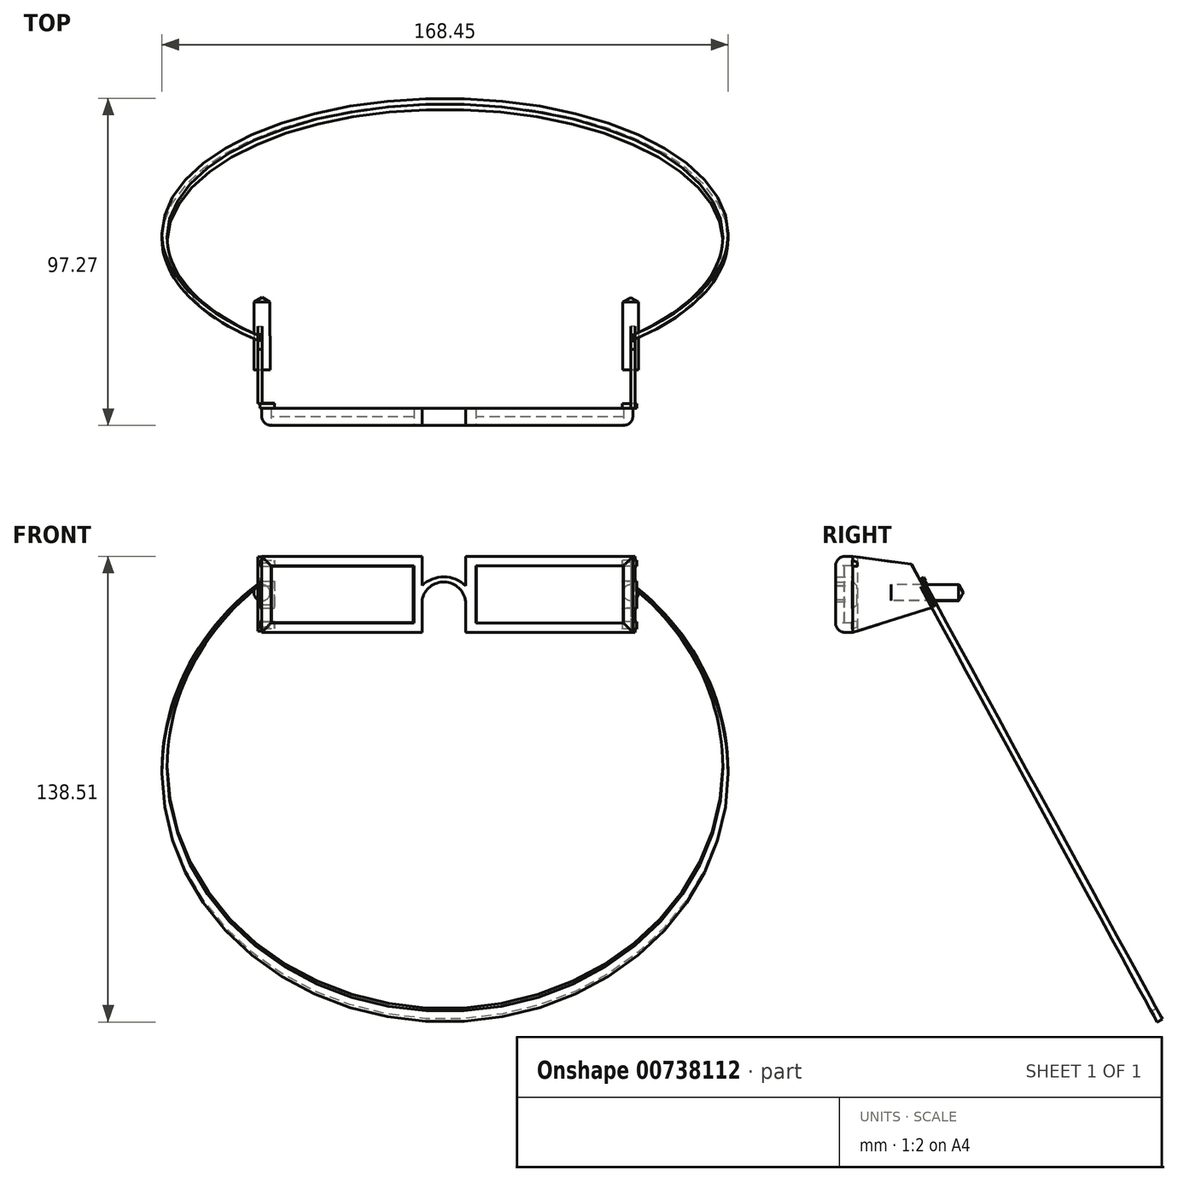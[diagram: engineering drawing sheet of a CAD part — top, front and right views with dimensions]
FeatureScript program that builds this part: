
annotation { "Feature Type Name" : "Feature", "Feature Type Description" : "" }
export const myFeature = defineFeature(function(context is Context, id is Id, definition is map)
    precondition{}
    {
        {
            var Q0;
            Q0=qCreatedBy(makeId("Front.planeOp"),FACE);
            var sketch = newSketch(context, id + "F0", { "sketchPlane" : qUnion([Q0])});
            skLineSegment(sketch, "E0.bottom", {"start": v(-53.68, 22.6) * mm, "end": v(-5.9, 22.6) * mm});
            skLineSegment(sketch, "E0.top", {"start": v(-53.68, 0) * mm, "end": v(-5.9, 0) * mm});
            skLineSegment(sketch, "E0.left", {"start": v(-53.68, 22.6) * mm, "end": v(-53.68, 0) * mm});
            skLineSegment(sketch, "E0.right", {"start": v(-5.9, 22.6) * mm, "end": v(-5.9, 0) * mm});
            skPoint(sketch, "E1.firstSnap0", {"position": v(-29.79, 22.6) * mm});
            skLineSegment(sketch, "E1.bottom", {"start": v(7.05, 22.6) * mm, "end": v(56.84, 22.6) * mm});
            skLineSegment(sketch, "E1.top", {"start": v(7.05, 0) * mm, "end": v(56.84, 0) * mm});
            skLineSegment(sketch, "E1.left", {"start": v(7.05, 22.6) * mm, "end": v(7.05, 0) * mm});
            skLineSegment(sketch, "E1.right", {"start": v(56.84, 22.6) * mm, "end": v(56.84, 0) * mm});
            skArc(sketch, "E2", {"start": v(7.05, 13.84) * mm, "mid": v(0.6, 16.5) * mm, "end": v(-5.9, 13.96) * mm});
            skArc(sketch, "E3", {"start": v(7.05, 9.18) * mm, "mid": v(0.8, 14.97) * mm, "end": v(-5.9, 9.71) * mm});
            skSolve(sketch);
        }
        {
            var Q0;
            {var subQ3=sQuery(id+"F0.wireOp",EDGE,"E1.bottom");Q0=makeQuery(id+"F0.imprint","IMPRINT",FACE,{"disambiguationData":[TD([[makeQuery(id+"F0.imprint","IMPRINT",EDGE,{"derivedFrom":subQ3}),-1.0]])]});}
            var Q1;
            {var subQ1=sQuery(id+"F0.wireOp",EDGE,"E0.bottom");Q1=makeQuery(id+"F0.imprint","IMPRINT",FACE,{"disambiguationData":[TD([[makeQuery(id+"F0.imprint","IMPRINT",EDGE,{"derivedFrom":subQ1}),-1.0]])]});}
            var Q2;
            {var subQ0=sQuery(id+"F0.wireOp",EDGE,"E2");Q2=makeQuery(id+"F0.imprint","IMPRINT",FACE,{"disambiguationData":[TD([[makeQuery(id+"F0.imprint","IMPRINT",EDGE,{"derivedFrom":subQ0}),1.0]])]});}
            extrude(context, id + "F1", {"entities" : qUnion([Q0, Q1, Q2]), "depth" : 2.54 * mm, "offsetDistance" : 25.4 * mm, "hasSecondDirection" : true, "secondDirectionOppositeDirection" : true, "secondDirectionDepth" : 2.54 * mm});
        }
        {
            var Q0;
            Q0=makeQuery(id+"F1.opExtrude","CAP_EDGE",EDGE,{"disambiguationData":[OSD([sQuery(id+"F0.wireOp",EDGE,"E0.bottom")])],"isStart":false});
            var Q1;
            Q1=makeQuery(id+"F1.opExtrude","CAP_EDGE",EDGE,{"disambiguationData":[OSD([sQuery(id+"F0.wireOp",EDGE,"E0.left")])],"isStart":false});
            var Q2;
            Q2=makeQuery(id+"F1.opExtrude","CAP_EDGE",EDGE,{"disambiguationData":[OSD([sQuery(id+"F0.wireOp",EDGE,"E0.top")])],"isStart":false});
            var Q3;
            Q3=makeQuery(id+"F1.opExtrude","CAP_EDGE",EDGE,{"disambiguationData":[OSD([sQuery(id+"F0.wireOp",EDGE,"E1.bottom")])],"isStart":false});
            var Q4;
            Q4=makeQuery(id+"F1.opExtrude","CAP_EDGE",EDGE,{"disambiguationData":[OSD([sQuery(id+"F0.wireOp",EDGE,"E1.top")])],"isStart":false});
            var Q5;
            Q5=makeQuery(id+"F1.opExtrude","CAP_EDGE",EDGE,{"disambiguationData":[OSD([sQuery(id+"F0.wireOp",EDGE,"E1.right")])],"isStart":false});
            fillet(context, id + "F2", {"entities" : qUnion([Q0, Q1, Q2, Q3, Q4, Q5]), "radius" : 2.8 * mm, "tangentPropagation" : true, "allowEdgeOverflow" : false});
        }
        {
            var Q0;
            Q0=makeQuery(id+"F1.opExtrude","CAP_FACE",FACE,{"disambiguationData":[OSD([sQuery(id+"F0.wireOp",EDGE,"E0.bottom"),sQuery(id+"F0.wireOp",EDGE,"E0.top"),sQuery(id+"F0.wireOp",EDGE,"E0.left"),sQuery(id+"F0.wireOp",EDGE,"E0.right"),sQuery(id+"F0.wireOp",EDGE,"E1.bottom"),sQuery(id+"F0.wireOp",EDGE,"E1.top"),sQuery(id+"F0.wireOp",EDGE,"E1.left"),sQuery(id+"F0.wireOp",EDGE,"E1.right"),sQuery(id+"F0.wireOp",EDGE,"E2"),sQuery(id+"F0.wireOp",EDGE,"E3")])],"isStart":false});
            var sketch = newSketch(context, id + "F3", { "sketchPlane" : qUnion([Q0])});
            skLineSegment(sketch, "E4", {"start": v(-8.32, 19.8) * mm, "end": v(-8.32, 2.8) * mm});
            skLineSegment(sketch, "E5", {"start": v(-8.32, 2.8) * mm, "end": v(-50.88, 2.8) * mm});
            skLineSegment(sketch, "E6", {"start": v(-50.88, 2.8) * mm, "end": v(-50.88, 19.8) * mm});
            skLineSegment(sketch, "E7", {"start": v(-50.88, 19.8) * mm, "end": v(-8.32, 19.8) * mm});
            skLineSegment(sketch, "E8", {"start": v(10.1, 2.8) * mm, "end": v(10.1, 19.8) * mm});
            skLineSegment(sketch, "E9", {"start": v(10.1, 19.8) * mm, "end": v(54.05, 19.8) * mm});
            skLineSegment(sketch, "E10", {"start": v(54.05, 19.8) * mm, "end": v(54.05, 2.8) * mm});
            skLineSegment(sketch, "E11", {"start": v(54.05, 2.8) * mm, "end": v(10.1, 2.8) * mm});
            skSolve(sketch);
        }
        {
            var Q0;
            Q0=makeQuery(id+"F3.imprint","IMPRINT",FACE,{"disambiguationData":[TD([[makeQuery(id+"F3.imprint","IMPRINT",EDGE,{"derivedFrom":sQuery(id+"F3.wireOp",EDGE,"E4")}),-1.0]])]});
            var Q1;
            Q1=makeQuery(id+"F3.imprint","IMPRINT",FACE,{"disambiguationData":[TD([[makeQuery(id+"F3.imprint","IMPRINT",EDGE,{"derivedFrom":sQuery(id+"F3.wireOp",EDGE,"E8")}),-1.0]])]});
            extrude(context, id + "F4", {"entities" : qUnion([Q0, Q1]), "operationType" : NewBodyOperationType.REMOVE, "oppositeDirection" : true, "depth" : 6.35 * mm, "offsetDistance" : 25.4 * mm});
        }
        {
            var Q0;
            Q0=makeQuery(id+"F1.opExtrude","SWEPT_FACE",FACE,{"disambiguationData":[OSD([sQuery(id+"F0.wireOp",EDGE,"E1.right")])]});
            var sketch = newSketch(context, id + "F5", { "sketchPlane" : qUnion([Q0])});
            skLineSegment(sketch, "E12", {"start": v(2.54, 22.6) * mm, "end": v(20.03, 20.27) * mm});
            skLineSegment(sketch, "E13", {"start": v(20.03, 20.27) * mm, "end": v(26.92, 7.57) * mm});
            skLineSegment(sketch, "E14", {"start": v(26.92, 7.57) * mm, "end": v(2.54, 0) * mm});
            skLineSegment(sketch, "E15", {"start": v(2.54, 0) * mm, "end": v(2.54, 22.6) * mm});
            skLineSegment(sketch, "E16", {"start": v(3.97, 22.4) * mm, "end": v(3.97, 0.44) * mm});
            skLineSegment(sketch, "E17", {"start": v(3.97, 0.44) * mm, "end": v(2.54, 0) * mm});
            skLineSegment(sketch, "E18", {"start": v(2.54, 22.6) * mm, "end": v(3.97, 22.4) * mm});
            skSolve(sketch);
        }
        {
            var Q0;
            Q0=makeQuery(id+"F5.imprint","IMPRINT",FACE,{"disambiguationData":[TD([[makeQuery(id+"F5.imprint","IMPRINT",EDGE,{"derivedFrom":sQuery(id+"F5.wireOp",EDGE,"E12")}),-1.0]])]});
            extrude(context, id + "F6", {"entities" : qUnion([Q0]), "depth" : 0.64 * mm, "offsetDistance" : 25.4 * mm, "hasSecondDirection" : true, "secondDirectionOppositeDirection" : true, "secondDirectionDepth" : 0.64 * mm});
        }
        {
            var Q0;
            Q0=makeQuery(id+"F6.opExtrude","CAP_FACE",FACE,{"disambiguationData":[OSD([sQuery(id+"F5.wireOp",EDGE,"E12"),sQuery(id+"F5.wireOp",EDGE,"E13"),sQuery(id+"F5.wireOp",EDGE,"E14"),sQuery(id+"F5.wireOp",EDGE,"E16")])],"isStart":false});
            var sketch = newSketch(context, id + "F7", { "sketchPlane" : qUnion([Q0])});
            skLineSegment(sketch, "E19", {"start": v(2.49, 21.39) * mm, "end": v(3.97, 20.75) * mm});
            skLineSegment(sketch, "E20", {"start": v(3.97, 20.75) * mm, "end": v(3.97, 19.64) * mm});
            skLineSegment(sketch, "E21", {"start": v(3.97, 19.64) * mm, "end": v(2.49, 19.64) * mm});
            skLineSegment(sketch, "E22", {"start": v(2.49, 19.64) * mm, "end": v(2.49, 21.39) * mm});
            skLineSegment(sketch, "E23", {"start": v(2.49, 15.2) * mm, "end": v(2.49, 7.14) * mm});
            skLineSegment(sketch, "E24", {"start": v(2.49, 7.14) * mm, "end": v(3.97, 8.29) * mm});
            skLineSegment(sketch, "E25", {"start": v(3.97, 8.29) * mm, "end": v(3.97, 13.84) * mm});
            skLineSegment(sketch, "E26", {"start": v(3.97, 13.84) * mm, "end": v(2.49, 15.2) * mm});
            skLineSegment(sketch, "E27", {"start": v(2.49, 3.13) * mm, "end": v(2.49, 1.04) * mm});
            skLineSegment(sketch, "E28", {"start": v(2.49, 1.04) * mm, "end": v(3.97, 1.8) * mm});
            skLineSegment(sketch, "E29", {"start": v(3.97, 1.8) * mm, "end": v(3.97, 3.17) * mm});
            skLineSegment(sketch, "E30", {"start": v(3.97, 3.17) * mm, "end": v(2.49, 3.13) * mm});
            skSolve(sketch);
        }
        {
            var Q0;
            Q0=makeQuery(id+"F7.imprint","IMPRINT",FACE,{"disambiguationData":[TD([[makeQuery(id+"F7.imprint","IMPRINT",EDGE,{"derivedFrom":sQuery(id+"F7.wireOp",EDGE,"E19")}),-1.0]])]});
            var Q1;
            Q1=makeQuery(id+"F7.imprint","IMPRINT",FACE,{"disambiguationData":[TD([[makeQuery(id+"F7.imprint","IMPRINT",EDGE,{"derivedFrom":sQuery(id+"F7.wireOp",EDGE,"E23")}),1.0]])]});
            var Q2;
            Q2=makeQuery(id+"F7.imprint","IMPRINT",FACE,{"disambiguationData":[TD([[makeQuery(id+"F7.imprint","IMPRINT",EDGE,{"derivedFrom":sQuery(id+"F7.wireOp",EDGE,"E27")}),1.0]])]});
            extrude(context, id + "F8", {"entities" : qUnion([Q0, Q1, Q2]), "depth" : 0.5 * mm, "offsetDistance" : 25.4 * mm, "hasSecondDirection" : true, "secondDirectionOppositeDirection" : true, "secondDirectionDepth" : 3.8 * mm});
        }
        {
            var Q0;
            Q0=makeQuery(id+"F6.opExtrude","CAP_FACE",FACE,{"disambiguationData":[OSD([sQuery(id+"F5.wireOp",EDGE,"E12"),sQuery(id+"F5.wireOp",EDGE,"E13"),sQuery(id+"F5.wireOp",EDGE,"E14"),sQuery(id+"F5.wireOp",EDGE,"E16")])],"isStart":true});
            var sketch = newSketch(context, id + "F9", { "sketchPlane" : qUnion([Q0])});
            skLineSegment(sketch, "E31", {"start": v(-13.96, 14.18) * mm, "end": v(-13.96, 11.83) * mm});
            skLineSegment(sketch, "E32", {"start": v(-13.96, 11.83) * mm, "end": v(-35.47, 11.83) * mm});
            skLineSegment(sketch, "E33", {"start": v(-13.96, 14.18) * mm, "end": v(-34.1, 14.18) * mm});
            skLineSegment(sketch, "E34", {"start": v(-34.1, 14.18) * mm, "end": v(-35.47, 11.83) * mm});
            skSolve(sketch);
        }
        {
            var Q0;
            {var subQ0=sQuery(id+"F9.wireOp",EDGE,"E34");Q0=makeQuery(id+"F9.imprint","IMPRINT",FACE,{"disambiguationData":[TD([[makeQuery(id+"F9.imprint","IMPRINT",EDGE,{"derivedFrom":subQ0}),1.0]])]});}
            var Q1;
            {var subQ0=sQuery(id+"F9.wireOp",EDGE,"E31");Q1=makeQuery(id+"F9.imprint","IMPRINT",FACE,{"disambiguationData":[TD([[makeQuery(id+"F9.imprint","IMPRINT",EDGE,{"derivedFrom":subQ0}),-1.0]])]});}
            var Q2;
            Q2=sQuery(id+"F9.wireOp",EDGE,"E32");
            revolve(context, id + "F10", {"surfaceOperationType" : NewSurfaceOperationType.NEW, "entities" : qUnion([Q0, Q1]), "axis" : qUnion([Q2]), "revolveType" : RevolveType.FULL});
        }
        {
            var Q0;
            Q0=makeQuery(id+"F1.opExtrude","SWEPT_FACE",FACE,{"disambiguationData":[OSD([sQuery(id+"F0.wireOp",EDGE,"E0.left")])]});
            var sketch = newSketch(context, id + "F11", { "sketchPlane" : qUnion([Q0])});
            skLineSegment(sketch, "E35", {"start": v(-2.54, 15.24) * mm, "end": v(-2.54, 7.18) * mm});
            skLineSegment(sketch, "E36", {"start": v(-2.54, 7.18) * mm, "end": v(-3.9, 8.29) * mm});
            skLineSegment(sketch, "E37", {"start": v(-3.9, 8.29) * mm, "end": v(-3.9, 13.88) * mm});
            skLineSegment(sketch, "E38", {"start": v(-3.9, 13.88) * mm, "end": v(-2.54, 15.24) * mm});
            skLineSegment(sketch, "E39", {"start": v(-2.54, 3.25) * mm, "end": v(-2.54, 1.08) * mm});
            skLineSegment(sketch, "E40", {"start": v(-2.54, 1.08) * mm, "end": v(-4.03, 1.59) * mm});
            skLineSegment(sketch, "E41", {"start": v(-4.03, 1.59) * mm, "end": v(-4.03, 3.21) * mm});
            skLineSegment(sketch, "E42", {"start": v(-4.03, 3.21) * mm, "end": v(-2.54, 3.25) * mm});
            skLineSegment(sketch, "E43", {"start": v(-3.9, 20.7) * mm, "end": v(-3.9, 19.68) * mm});
            skLineSegment(sketch, "E44", {"start": v(-3.9, 19.68) * mm, "end": v(-2.54, 19.68) * mm});
            skLineSegment(sketch, "E45", {"start": v(-3.9, 20.7) * mm, "end": v(-2.54, 21.43) * mm});
            skLineSegment(sketch, "E46", {"start": v(-2.54, 21.43) * mm, "end": v(-2.54, 19.68) * mm});
            skSolve(sketch);
        }
        {
            var Q0;
            Q0=makeQuery(id+"F11.imprint","IMPRINT",FACE,{"disambiguationData":[TD([[makeQuery(id+"F11.imprint","IMPRINT",EDGE,{"derivedFrom":sQuery(id+"F11.wireOp",EDGE,"E36")}),-1.0]])]});
            var Q1;
            Q1=makeQuery(id+"F11.imprint","IMPRINT",FACE,{"disambiguationData":[TD([[makeQuery(id+"F11.imprint","IMPRINT",EDGE,{"derivedFrom":sQuery(id+"F11.wireOp",EDGE,"E43")}),1.0]])]});
            var Q2;
            Q2=makeQuery(id+"F11.imprint","IMPRINT",FACE,{"disambiguationData":[TD([[makeQuery(id+"F11.imprint","IMPRINT",EDGE,{"derivedFrom":sQuery(id+"F11.wireOp",EDGE,"E39")}),-1.0]])]});
            extrude(context, id + "F12", {"entities" : qUnion([Q0, Q1, Q2]), "depth" : 0.5 * mm, "offsetDistance" : 25.4 * mm, "hasSecondDirection" : true, "secondDirectionOppositeDirection" : true, "secondDirectionDepth" : 3.8 * mm});
        }
        {
            var Q0;
            Q0=makeQuery(id+"F12.opExtrude","CAP_FACE",FACE,{"disambiguationData":[OSD([sQuery(id+"F11.wireOp",EDGE,"E36"),sQuery(id+"F11.wireOp",EDGE,"E37"),sQuery(id+"F11.wireOp",EDGE,"E38"),sQuery(id+"F11.wireOp",EDGE,"E35")])],"isStart":false});
            var sketch = newSketch(context, id + "F13", { "sketchPlane" : qUnion([Q0])});
            skLineSegment(sketch, "E47", {"start": v(-3.98, 22.42) * mm, "end": v(-3.98, 0.42) * mm});
            skLineSegment(sketch, "E48", {"start": v(-3.98, 0.42) * mm, "end": v(-26.94, 7.63) * mm});
            skLineSegment(sketch, "E49", {"start": v(-26.94, 7.63) * mm, "end": v(-20.07, 20.25) * mm});
            skLineSegment(sketch, "E50", {"start": v(-20.07, 20.25) * mm, "end": v(-3.98, 22.42) * mm});
            skSolve(sketch);
        }
        {
            var Q0;
            Q0=makeQuery(id+"F13.imprint","IMPRINT",FACE,{"disambiguationData":[TD([[makeQuery(id+"F13.imprint","IMPRINT",EDGE,{"derivedFrom":sQuery(id+"F13.wireOp",EDGE,"E47")}),-1.0]])]});
            extrude(context, id + "F14", {"entities" : qUnion([Q0]), "depth" : 0.64 * mm, "offsetDistance" : 25.4 * mm, "hasSecondDirection" : true, "secondDirectionOppositeDirection" : true, "secondDirectionDepth" : 0.64 * mm});
        }
        {
            var Q0;
            Q0=makeQuery(id+"F14.opExtrude","CAP_FACE",FACE,{"disambiguationData":[OSD([sQuery(id+"F13.wireOp",EDGE,"E47"),sQuery(id+"F13.wireOp",EDGE,"E48"),sQuery(id+"F13.wireOp",EDGE,"E49"),sQuery(id+"F13.wireOp",EDGE,"E50")])],"isStart":true});
            var sketch = newSketch(context, id + "F15", { "sketchPlane" : qUnion([Q0])});
            skLineSegment(sketch, "E51", {"start": v(14, 14.2) * mm, "end": v(14, 11.8) * mm});
            skLineSegment(sketch, "E52", {"start": v(14, 11.8) * mm, "end": v(35.48, 11.8) * mm});
            skLineSegment(sketch, "E53", {"start": v(35.48, 11.8) * mm, "end": v(34.16, 14.18) * mm});
            skLineSegment(sketch, "E54", {"start": v(34.16, 14.18) * mm, "end": v(14, 14.2) * mm});
            skSolve(sketch);
        }
        {
            var Q0;
            {var subQ0=sQuery(id+"F15.wireOp",EDGE,"E51");Q0=makeQuery(id+"F15.imprint","IMPRINT",FACE,{"disambiguationData":[TD([[makeQuery(id+"F15.imprint","IMPRINT",EDGE,{"derivedFrom":subQ0}),1.0]])]});}
            var Q1;
            {var subQ0=sQuery(id+"F15.wireOp",EDGE,"E53");Q1=makeQuery(id+"F15.imprint","IMPRINT",FACE,{"disambiguationData":[TD([[makeQuery(id+"F15.imprint","IMPRINT",EDGE,{"derivedFrom":subQ0}),1.0]])]});}
            var Q2;
            Q2=sQuery(id+"F15.wireOp",EDGE,"E52");
            revolve(context, id + "F16", {"surfaceOperationType" : NewSurfaceOperationType.NEW, "entities" : qUnion([Q0, Q1]), "axis" : qUnion([Q2]), "revolveType" : RevolveType.FULL});
        }
        {
            var Q0;
            Q0=makeQuery(id+"F14.opExtrude","SWEPT_FACE",FACE,{"disambiguationData":[OSD([sQuery(id+"F13.wireOp",EDGE,"E49")])]});
            var sketch = newSketch(context, id + "F17", { "sketchPlane" : qUnion([Q0])});
            skLineSegment(sketch, "E55", {"start": v(53.85, 1.29) * mm, "end": v(53.85, 2.6) * mm});
            skLineSegment(sketch, "E56", {"start": v(53.85, 2.6) * mm, "end": v(54.57, 2.6) * mm});
            skLineSegment(sketch, "E57", {"start": v(54.57, 2.6) * mm, "end": v(54.57, 1.01) * mm});
            skLineSegment(sketch, "E58", {"start": v(54.57, 1.01) * mm, "end": v(53.85, 1.29) * mm});
            skSolve(sketch);
        }
        {
            var Q0;
            Q0=makeQuery(id+"F17.imprint","IMPRINT",FACE,{"disambiguationData":[TD([[makeQuery(id+"F17.imprint","IMPRINT",EDGE,{"derivedFrom":sQuery(id+"F17.wireOp",EDGE,"E55")}),-1.0]])]});
            extrude(context, id + "F18", {"entities" : qUnion([Q0]), "depth" : 1.27 * mm, "offsetDistance" : 25.4 * mm});
        }
        {
            var Q0;
            Q0=makeQuery(id+"F18.opExtrude","SWEPT_FACE",FACE,{"disambiguationData":[OSD([sQuery(id+"F17.wireOp",EDGE,"E55")])]});
            var sketch = newSketch(context, id + "F19", { "sketchPlane" : qUnion([Q0])});
            skCircle(sketch, "E59", {"center": v(23.52, 15.2) * mm, "radius": 0.25 * mm});
            skSolve(sketch);
        }
        {
            var Q0;
            Q0=makeQuery(id+"F19.imprint","IMPRINT",FACE,{"disambiguationData":[TD([[makeQuery(id+"F19.imprint","IMPRINT",EDGE,{"derivedFrom":sQuery(id+"F19.wireOp",EDGE,"E59")}),1.0]])]});
            extrude(context, id + "F20", {"entities" : qUnion([Q0]), "operationType" : NewBodyOperationType.REMOVE, "oppositeDirection" : true, "depth" : 25.4 * mm, "offsetDistance" : 25.4 * mm});
        }
        {
            var Q0;
            Q0=makeQuery(id+"F6.opExtrude","SWEPT_FACE",FACE,{"disambiguationData":[OSD([sQuery(id+"F5.wireOp",EDGE,"E13")])]});
            var sketch = newSketch(context, id + "F21", { "sketchPlane" : qUnion([Q0])});
            skLineSegment(sketch, "E60", {"start": v(-57.15, 3.06) * mm, "end": v(-57.15, 1.89) * mm});
            skLineSegment(sketch, "E61", {"start": v(-57.15, 1.89) * mm, "end": v(-56.54, 1.89) * mm});
            skLineSegment(sketch, "E62", {"start": v(-56.54, 1.89) * mm, "end": v(-56.54, 2.73) * mm});
            skLineSegment(sketch, "E63", {"start": v(-56.54, 2.73) * mm, "end": v(-57.15, 3.06) * mm});
            skSolve(sketch);
        }
        {
            var Q0;
            Q0=makeQuery(id+"F21.imprint","IMPRINT",FACE,{"disambiguationData":[TD([[makeQuery(id+"F21.imprint","IMPRINT",EDGE,{"derivedFrom":sQuery(id+"F21.wireOp",EDGE,"E60")}),1.0]])]});
            extrude(context, id + "F22", {"entities" : qUnion([Q0]), "depth" : 1.35 * mm, "offsetDistance" : 25.4 * mm});
        }
        {
            var Q0;
            Q0=makeQuery(id+"F22.opExtrude","SWEPT_FACE",FACE,{"disambiguationData":[OSD([sQuery(id+"F21.wireOp",EDGE,"E60")])]});
            var sketch = newSketch(context, id + "F23", { "sketchPlane" : qUnion([Q0])});
            skCircle(sketch, "E64", {"center": v(23.33, 15.52) * mm, "radius": 0.22 * mm});
            skSolve(sketch);
        }
        {
            var Q0;
            Q0=makeQuery(id+"F23.imprint","IMPRINT",FACE,{"disambiguationData":[TD([[makeQuery(id+"F23.imprint","IMPRINT",EDGE,{"derivedFrom":sQuery(id+"F23.wireOp",EDGE,"E64")}),1.0]])]});
            extrude(context, id + "F24", {"entities" : qUnion([Q0]), "operationType" : NewBodyOperationType.REMOVE, "oppositeDirection" : true, "depth" : 25.4 * mm, "offsetDistance" : 25.4 * mm});
        }
        {
            var Q0;
            Q0=makeQuery(id+"F14.opExtrude","SWEPT_FACE",FACE,{"disambiguationData":[OSD([sQuery(id+"F13.wireOp",EDGE,"E49")])]});
            var sketch = newSketch(context, id + "F25", { "sketchPlane" : qUnion([Q0])});
            skArc(sketch, "E65", {"start": v(-56.65, 1.01) * mm, "mid": v(-0.92, -146.36) * mm, "end": v(54.82, 1.01) * mm});
            skPoint(sketch, "E65.startSnap0", {"position": v(54.82, 1.01) * mm});
            skArc(sketch, "E66", {"start": v(-56.65, 1.01) * mm, "mid": v(-0.92, -142.76) * mm, "end": v(54.82, 1.01) * mm});
            skSolve(sketch);
        }
        {
            var Q0;
            {var subQ0=sQuery(id+"F25.wireOp",EDGE,"E66");var subQ1=sQuery(id+"F25.wireOp",EDGE,"E65");var subQ2=makeQuery(id+"F25.imprint","INTERSECT",VERTEX,{"disambiguationData":[OD(0.0)],"derivedFrom":[subQ1,subQ0]});Q0=makeQuery(id+"F25.imprint","IMPRINT",FACE,{"disambiguationData":[TD([[makeQuery(id+"F25.imprint","IMPRINT",EDGE,{"disambiguationData":[TD([[subQ2,-1.0]])],"derivedFrom":subQ1}),1.0]])]});}
            extrude(context, id + "F26", {"entities" : qUnion([Q0]), "depth" : 0.89 * mm, "offsetDistance" : 25.4 * mm, "hasSecondDirection" : true, "secondDirectionOppositeDirection" : true, "secondDirectionDepth" : 0.89 * mm});
        }
        {
            var Q0;
            {var subQ1=sQuery(id+"F0.wireOp",EDGE,"E0.bottom");Q0=makeQuery(id+"F0.imprint","IMPRINT",FACE,{"disambiguationData":[TD([[makeQuery(id+"F0.imprint","IMPRINT",EDGE,{"derivedFrom":subQ1}),-1.0]])]});}
            var sketch = newSketch(context, id + "F27", { "sketchPlane" : qUnion([Q0])});
            skLineSegment(sketch, "E67", {"start": v(-50.77, 19.64) * mm, "end": v(-50.77, 2.88) * mm});
            skLineSegment(sketch, "E68", {"start": v(-50.77, 2.88) * mm, "end": v(-8.49, 2.88) * mm});
            skLineSegment(sketch, "E69", {"start": v(-8.49, 2.88) * mm, "end": v(-8.49, 19.7) * mm});
            skLineSegment(sketch, "E70", {"start": v(-8.49, 19.7) * mm, "end": v(-50.77, 19.64) * mm});
            skLineSegment(sketch, "E71", {"start": v(10.2, 19.86) * mm, "end": v(10.2, 2.81) * mm});
            skLineSegment(sketch, "E72", {"start": v(10.2, 2.81) * mm, "end": v(53.97, 2.81) * mm});
            skLineSegment(sketch, "E73", {"start": v(53.97, 2.81) * mm, "end": v(53.97, 19.75) * mm});
            skLineSegment(sketch, "E74", {"start": v(53.97, 19.75) * mm, "end": v(10.2, 19.86) * mm});
            skSolve(sketch);
        }
        {
            var Q0;
            Q0=makeQuery(id+"F27.imprint","IMPRINT",FACE,{"disambiguationData":[TD([[makeQuery(id+"F27.imprint","IMPRINT",EDGE,{"derivedFrom":sQuery(id+"F27.wireOp",EDGE,"E67")}),1.0]])]});
            var Q1;
            Q1=makeQuery(id+"F27.imprint","IMPRINT",FACE,{"disambiguationData":[TD([[makeQuery(id+"F27.imprint","IMPRINT",EDGE,{"derivedFrom":sQuery(id+"F27.wireOp",EDGE,"E71")}),1.0]])]});
            extrude(context, id + "F28", {"entities" : qUnion([Q0, Q1]), "depth" : 0.03 * mm, "offsetDistance" : 25.4 * mm, "hasSecondDirection" : true, "secondDirectionOppositeDirection" : true, "secondDirectionDepth" : 0.03 * mm});
        }
    });
